# Revit family: SUBACUATICA_SLNSA_U_W_N_C
name_source: partatom
category: Luminarias
units: mm (PartAtom-declared; Revit-internal decimal feet)

## family parameters
Compartido = No
Corte con vacíos al cargar = No
Cota de conector redondo = Diámetro de uso
Origen de luz = Sí
Punto de cálculo de habitación = No
Se basa en plano de trabajo = Sí
Siempre vertical = No
Tipo de pieza = Normal

## types (4) — shared parameters
Cambio de temperatura de color de luz atenuada = <Ninguno>
Comentarios de vataje = 24
Fabricante = BRILLANT
Filtro de color = 16777215
Longitud de línea de emisión = 600 mm
Marca = BRILLANT
Tamaño de símbolo de origen de luz = 610 mm
zero-valued in all types: Elevación por defecto

## per-type parameters (varying)
| type | Descripción | Modelo |
| SUBACUATICA_SLNSA.U | TIRA LED SUBACUATICA HECHA DE SILICON CON UNA POTENCIA DE 4.8W/M, USO PARA EXTERIORES O ALBERCAS IP68, IRC 80, TEMPERATURA EN BLANCO CALIDO 2700K, 450 LUMENES/M, PRESENTACION DE 25M Y LOS CORTES DEBEN DE SER SOLICITADOS DESDE ORIGEN PARA GARANTIZAR EL SELLADO, PROFUNDAID MAXIMA DE 2M, RESISTENTE A SOLUCIONES SALINAS, A CLORO, FUEGO Y RAYOS UV. ALIMENTADO A 24V, REQUIERE ACCESORIOS. | SLNSA.U |
| SUBACUATICA_SLNSA.W | TIRA LED SUBACUATICA HECHA DE SILICON CON UNA POTENCIA DE 4.8W/M, USO PARA EXTERIORES O ALBERCAS IP68, IRC 80, TEMPERATURA EN BLANCO CALIDO 3000K, 450 LUMENES/M, PRESENTACION DE 25M Y LOS CORTES DEBEN DE SER SOLICITADOS DESDE ORIGEN PARA GARANTIZAR EL SELLADO, PROFUNDAID MAXIMA DE 2M, RESISTENTE A SOLUCIONES SALINAS, A CLORO, FUEGO Y RAYOS UV. ALIMENTADO A 24V, REQUIERE ACCESORIOS. | SLNSA.W |
| SUBACUATICA_SLNSA.N | TIRA LED SUBACUATICA HECHA DE SILICON CON UNA POTENCIA DE 4.8W/M, USO PARA EXTERIORES O ALBERCAS IP68, IRC 80, TEMPERATURA EN BLANCO NEUTRO 4000K, 450 LUMENES/M, PRESENTACION DE 25M Y LOS CORTES DEBEN DE SER SOLICITADOS DESDE ORIGEN PARA GARANTIZAR EL SELLADO, PROFUNDAID MAXIMA DE 2M, RESISTENTE A SOLUCIONES SALINAS, A CLORO, FUEGO Y RAYOS UV. ALIMENTADO A 24V, REQUIERE ACCESORIOS. | SLNSA.N |
| SUBACUATICA_SLNSA.C | TIRA LED SUBACUATICA HECHA DE SILICON CON UNA POTENCIA DE 4.8W/M, USO PARA EXTERIORES O ALBERCAS IP68, IRC 80, TEMPERATURA EN BLANCO FRIO 6000K, 450 LUMENES/M, PRESENTACION DE 25M Y LOS CORTES DEBEN DE SER SOLICITADOS DESDE ORIGEN PARA GARANTIZAR EL SELLADO, PROFUNDAID MAXIMA DE 2M, RESISTENTE A SOLUCIONES SALINAS, A CLORO, FUEGO Y RAYOS UV. ALIMENTADO A 24V, REQUIERE ACCESORIOS. | SLNSA.C |

## geometry (parser evidence)
native form markers: Blend x2
no freeform markers — native parametric forms only
